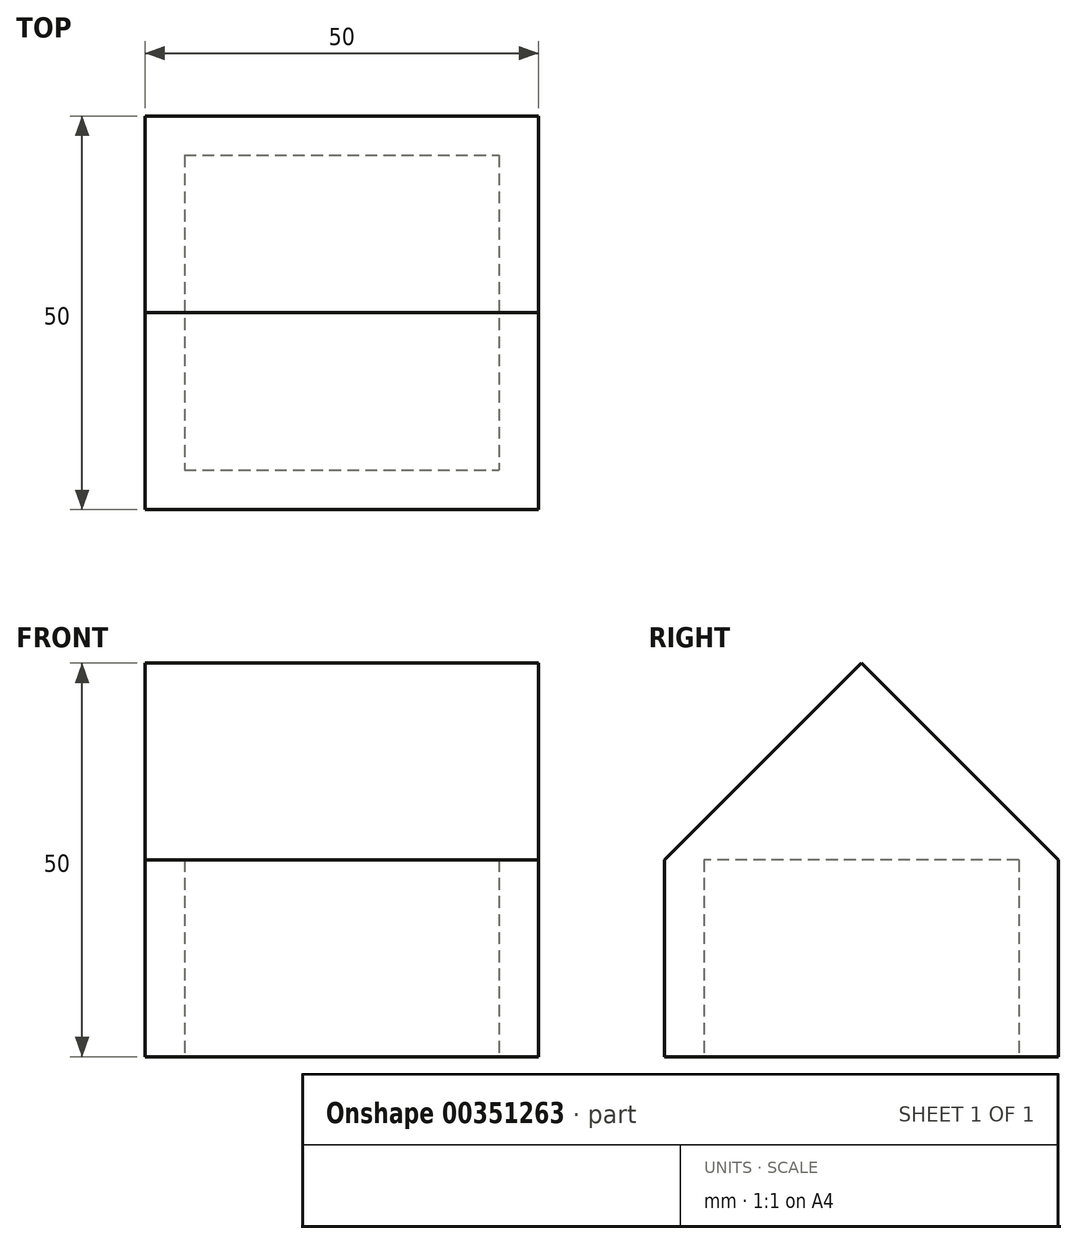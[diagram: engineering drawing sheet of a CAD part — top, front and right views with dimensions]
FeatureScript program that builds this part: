
annotation { "Feature Type Name" : "Feature", "Feature Type Description" : "" }
export const myFeature = defineFeature(function(context is Context, id is Id, definition is map)
    precondition{}
    {
        {
            var Q0;
            Q0=qCreatedBy(makeId("Top.planeOp"),FACE);
            var sketch = newSketch(context, id + "F0", { "sketchPlane" : qUnion([Q0])});
            skLineSegment(sketch, "E0.bottom", {"start": v(0, 0) * mm, "end": v(50, 0) * mm});
            skLineSegment(sketch, "E0.top", {"start": v(0, 50) * mm, "end": v(50, 50) * mm});
            skLineSegment(sketch, "E0.left", {"start": v(0, 0) * mm, "end": v(0, 50) * mm});
            skLineSegment(sketch, "E0.right", {"start": v(50, 0) * mm, "end": v(50, 50) * mm});
            skLineSegment(sketch, "E1.bottom", {"start": v(5, 45) * mm, "end": v(45, 45) * mm});
            skLineSegment(sketch, "E1.top", {"start": v(5, 5) * mm, "end": v(45, 5) * mm});
            skLineSegment(sketch, "E1.left", {"start": v(5, 45) * mm, "end": v(5, 5) * mm});
            skLineSegment(sketch, "E1.right", {"start": v(45, 45) * mm, "end": v(45, 5) * mm});
            skPoint(sketch, "E1.middle", {"position": v(25, 25) * mm});
            skLineSegment(sketch, "E2", {"start": v(25, 25) * mm, "end": v(25, 50) * mm, "construction": true});
            skLineSegment(sketch, "E3", {"start": v(25, 25) * mm, "end": v(0, 25) * mm, "construction": true});
            skSolve(sketch);
        }
        {
            var Q0;
            Q0 = qSketchRegion(id + "F0", true);
            extrude(context, id + "F1", {"entities" : qUnion([Q0]), "depth" : 25 * mm});
        }
        {
            var Q0;
            Q0=makeQuery(id+"F1.opExtrude","CAP_FACE",FACE,{"disambiguationData":[OSD([sQuery(id+"F0.wireOp",EDGE,"E0.bottom"),sQuery(id+"F0.wireOp",EDGE,"E0.top"),sQuery(id+"F0.wireOp",EDGE,"E0.left"),sQuery(id+"F0.wireOp",EDGE,"E0.right"),sQuery(id+"F0.wireOp",EDGE,"E1.bottom"),sQuery(id+"F0.wireOp",EDGE,"E1.top"),sQuery(id+"F0.wireOp",EDGE,"E1.left"),sQuery(id+"F0.wireOp",EDGE,"E1.right")])],"isStart":false});
            var sketch = newSketch(context, id + "F2", { "sketchPlane" : qUnion([Q0])});
            skLineSegment(sketch, "E4.bottom", {"start": v(0, 50) * mm, "end": v(50, 50) * mm});
            skLineSegment(sketch, "E4.top", {"start": v(0, 0) * mm, "end": v(50, 0) * mm});
            skLineSegment(sketch, "E4.left", {"start": v(0, 50) * mm, "end": v(0, 0) * mm});
            skLineSegment(sketch, "E4.right", {"start": v(50, 50) * mm, "end": v(50, 0) * mm});
            skSolve(sketch);
        }
        {
            var Q0;
            Q0=makeQuery(id+"F2.imprint","IMPRINT",FACE,{"disambiguationData":[TD([[makeQuery(id+"F2.imprint","IMPRINT",EDGE,{"derivedFrom":sQuery(id+"F2.wireOp",EDGE,"E4.bottom")}),-1.0]])]});
            var Q1;
            Q1=makeQuery(id+"F2.imprint","IMPRINT",FACE,{"disambiguationData":[TD([[makeQuery(id+"F2.imprint","IMPRINT",EDGE,{"derivedFrom":makeQuery(id+"F1.opExtrude","CAP_EDGE",EDGE,{"disambiguationData":[OSD([sQuery(id+"F0.wireOp",EDGE,"E1.bottom")])],"isStart":false})}),-1.0]])]});
            extrude(context, id + "F3", {"entities" : qUnion([Q0, Q1]), "operationType" : NewBodyOperationType.ADD, "depth" : 25 * mm});
        }
        {
            var Q0;
            Q0=makeQuery(id+"F3.opExtrude","CAP_EDGE",EDGE,{"disambiguationData":[OSD([sQuery(id+"F2.wireOp",EDGE,"E4.top")])],"isStart":false});
            var Q1;
            Q1=makeQuery(id+"F3.opExtrude","CAP_EDGE",EDGE,{"disambiguationData":[OSD([sQuery(id+"F2.wireOp",EDGE,"E4.bottom")])],"isStart":false});
            chamfer(context, id + "F4", {"entities" : qUnion([Q0, Q1]), "width" : 25 * mm, "tangentPropagation" : true});
        }
    });
